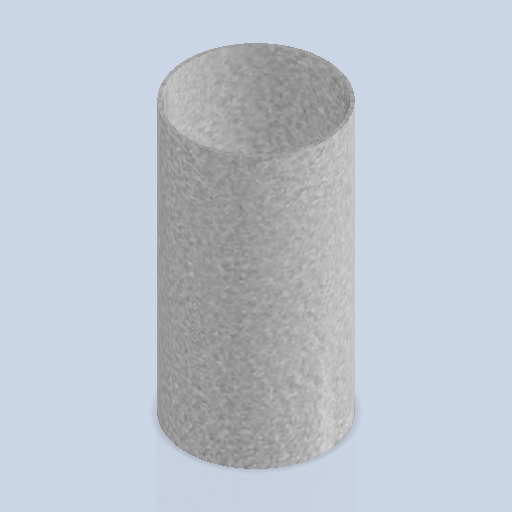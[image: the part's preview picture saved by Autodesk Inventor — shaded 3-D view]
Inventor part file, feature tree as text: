
AUTODESK INVENTOR PART (.ipt)
format: ipt  version: 2024.2 (Build 282272000, 272)  size: 236,032 bytes
history: native  units: mm
features: sketch x2, revolve x1, extrude x1
ambient origin geometry x8: Origin, YZ Plane, XZ Plane, XY Plane, X Axis, Y Axis, Z Axis, Center Point
bodies: Volumenkörper1 (feature_tree)
feature tree (4):
  revolve  "Umdrehung1"
  extrude  "Extrusion1"  Depth=127.5mm
  sketch  "Skizze1"  dims[d0=127.5mm d4=66.0mm]
  sketch  "Skizze3"  dims[d5=90.0deg d7=63.0mm d8=10.0mm d9=0.0mm]
